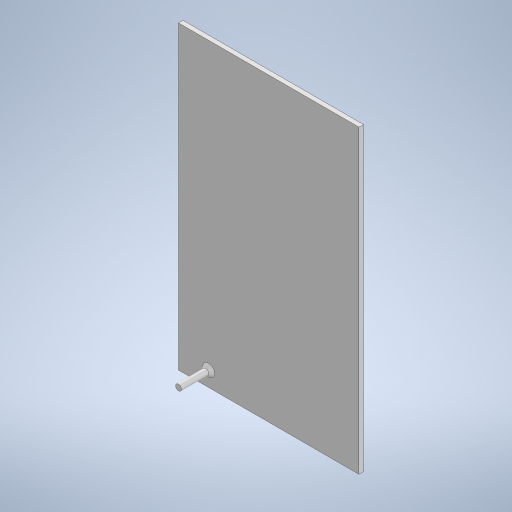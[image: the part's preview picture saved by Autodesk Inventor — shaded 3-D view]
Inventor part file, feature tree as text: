
AUTODESK INVENTOR PART (.ipt)
format: ipt  version: 2024 (Build 280153000, 153)  size: 249,856 bytes
history: native  units: mm
features: extrude x2, sketch x2, chamfer x1
ambient origin geometry x8: Origin, YZ Plane, XZ Plane, XY Plane, X Axis, Y Axis, Z Axis, Center Point
bodies: Solid1 (feature_tree)
feature tree (5):
  extrude  "Extrusion1"  Depth=120.0mm
  extrude  "Extrusion2"  Depth=2.0mm
  chamfer  "Chamfer1"  Distance=10.0mm
  sketch  "Sketch1"  dims[d1=200.0mm d2=120.0mm]
  sketch  "Sketch2"  dims[d3=3.0mm d4=0.0mm d5=4.0mm d6=10.0mm d7=20.0mm d8=20.0mm d9=0.0mm d10=2.0mm d11=2.0mm d12=45.0deg]
